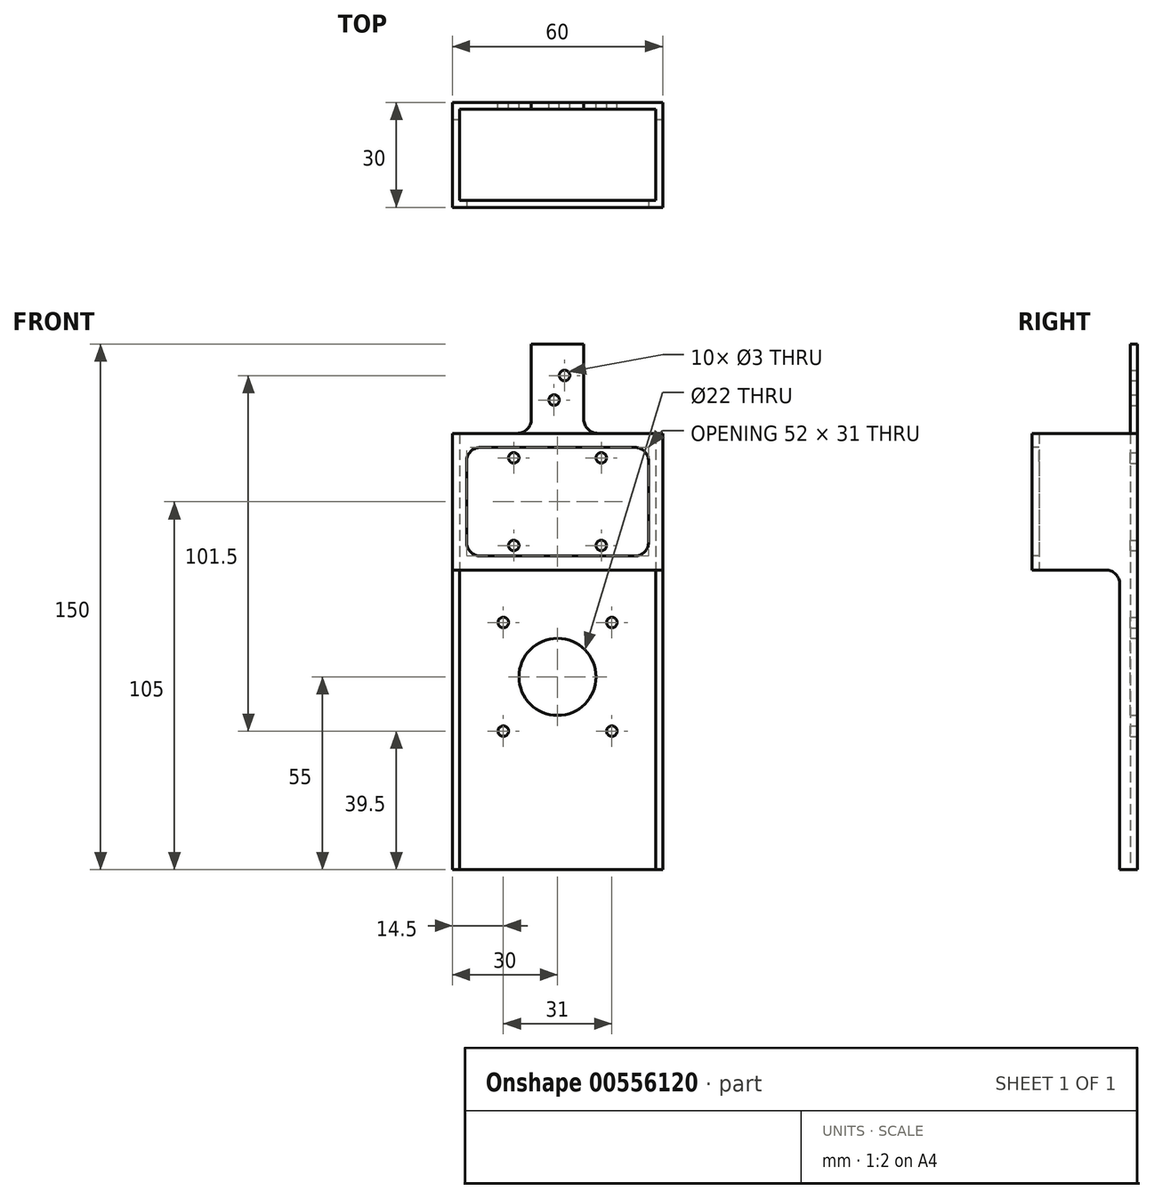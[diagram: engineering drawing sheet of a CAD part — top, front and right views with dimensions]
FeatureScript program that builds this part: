
annotation { "Feature Type Name" : "Feature", "Feature Type Description" : "" }
export const myFeature = defineFeature(function(context is Context, id is Id, definition is map)
    precondition{}
    {
        {
            var Q0;
            Q0=qCreatedBy(makeId("Top.planeOp"),FACE);
            var sketch = newSketch(context, id + "F0", { "sketchPlane" : qUnion([Q0])});
            skLineSegment(sketch, "E0.bottom", {"start": v(30, 15) * mm, "end": v(-30, 15) * mm});
            skLineSegment(sketch, "E0.top", {"start": v(30, -15) * mm, "end": v(-30, -15) * mm});
            skLineSegment(sketch, "E0.left", {"start": v(30, 15) * mm, "end": v(30, -15) * mm});
            skLineSegment(sketch, "E0.right", {"start": v(-30, 15) * mm, "end": v(-30, -15) * mm});
            skPoint(sketch, "E0.middle", {"position": v(0, 0) * mm});
            skSolve(sketch);
        }
        {
            var Q0;
            Q0 = qSketchRegion(id + "F0", true);
            extrude(context, id + "F1", {"entities" : qUnion([Q0]), "depth" : 150 * mm, "offsetDistance" : 25 * mm});
        }
        {
            var Q0;
            Q0=makeQuery(id+"F1.opExtrude","CAP_FACE",FACE,{"disambiguationData":[OSD([sQuery(id+"F0.wireOp",EDGE,"E0.bottom"),sQuery(id+"F0.wireOp",EDGE,"E0.top"),sQuery(id+"F0.wireOp",EDGE,"E0.left"),sQuery(id+"F0.wireOp",EDGE,"E0.right")])],"isStart":false});
            var Q1;
            Q1=makeQuery(id+"F1.opExtrude","CAP_FACE",FACE,{"disambiguationData":[OSD([sQuery(id+"F0.wireOp",EDGE,"E0.bottom"),sQuery(id+"F0.wireOp",EDGE,"E0.top"),sQuery(id+"F0.wireOp",EDGE,"E0.left"),sQuery(id+"F0.wireOp",EDGE,"E0.right")])],"isStart":true});
            shell(context, id + "F2", {"entities" : qUnion([Q0, Q1]), "thickness" : 2 * mm});
        }
        {
            var Q0;
            Q0=makeQuery(id+"F1.opExtrude","SWEPT_FACE",FACE,{"disambiguationData":[OSD([sQuery(id+"F0.wireOp",EDGE,"E0.bottom")])]});
            var sketch = newSketch(context, id + "F3", { "sketchPlane" : qUnion([Q0])});
            skLineSegment(sketch, "E1.bottom", {"start": v(12.5, 117.5) * mm, "end": v(-12.5, 117.5) * mm, "construction": true});
            skLineSegment(sketch, "E1.top", {"start": v(12.5, 92.5) * mm, "end": v(-12.5, 92.5) * mm, "construction": true});
            skLineSegment(sketch, "E1.left", {"start": v(12.5, 117.5) * mm, "end": v(12.5, 92.5) * mm, "construction": true});
            skLineSegment(sketch, "E1.right", {"start": v(-12.5, 117.5) * mm, "end": v(-12.5, 92.5) * mm, "construction": true});
            skPoint(sketch, "E1.middle", {"position": v(0, 105) * mm});
            skCircle(sketch, "E2", {"center": v(0, 55) * mm, "radius": 11 * mm});
            skLineSegment(sketch, "E3.bottom", {"start": v(15.5, 70.5) * mm, "end": v(-15.5, 70.5) * mm, "construction": true});
            skLineSegment(sketch, "E3.top", {"start": v(15.5, 39.5) * mm, "end": v(-15.5, 39.5) * mm, "construction": true});
            skLineSegment(sketch, "E3.left", {"start": v(15.5, 70.5) * mm, "end": v(15.5, 39.5) * mm, "construction": true});
            skLineSegment(sketch, "E3.right", {"start": v(-15.5, 70.5) * mm, "end": v(-15.5, 39.5) * mm, "construction": true});
            skLineSegment(sketch, "E4.top", {"start": v(-7.5, 125) * mm, "end": v(7.5, 125) * mm, "construction": true});
            skLineSegment(sketch, "E4.left", {"start": v(-7.5, 150) * mm, "end": v(-7.5, 125) * mm, "construction": true});
            skLineSegment(sketch, "E4.right", {"start": v(7.5, 150) * mm, "end": v(7.5, 125) * mm, "construction": true});
            skPoint(sketch, "E4.middle", {"position": v(0, 137.5) * mm});
            skLineSegment(sketch, "E5", {"start": v(1, 125) * mm, "end": v(1, 150) * mm, "construction": true});
            skLineSegment(sketch, "E6", {"start": v(-2, 125) * mm, "end": v(-2, 150) * mm, "construction": true});
            skPoint(sketch, "E7", {"position": v(-2, 141) * mm});
            skPoint(sketch, "E8", {"position": v(1, 134) * mm});
            skSolve(sketch);
        }
        {
            var Q0;
            Q0=sQuery(id+"F3.wireOp",VERTEX,"E1.right.start");
            var Q1;
            Q1=sQuery(id+"F3.wireOp",VERTEX,"E1.bottom.start");
            var Q2;
            Q2=sQuery(id+"F3.wireOp",VERTEX,"E1.right.end");
            var Q3;
            Q3=sQuery(id+"F3.wireOp",VERTEX,"E1.left.end");
            var Q4;
            Q4=makeQuery(id+"F1.opExtrude","SWEPT_BODY",BODY,{"disambiguationData":[OSD([sQuery(id+"F0.wireOp",EDGE,"E0.bottom"),sQuery(id+"F0.wireOp",EDGE,"E0.top"),sQuery(id+"F0.wireOp",EDGE,"E0.left"),sQuery(id+"F0.wireOp",EDGE,"E0.right")])]});
            hole(context, id + "F4", {"style" : HoleStyle.SIMPLE, "endStyle" : HoleEndStyle.THROUGH, "holeDiameter" : 3 * mm, "majorDiameter" : 5 * mm, "isTappedThrough" : true, "tappedDepth" : 12 * mm, "tapClearance" : 3, "startFromSketch" : true, "locations" : qUnion([Q0, Q1, Q2, Q3]), "scope" : qUnion([Q4])});
        }
        {
            var Q0;
            Q0=makeQuery(id+"F3.imprint","IMPRINT",FACE,{"disambiguationData":[TD([[makeQuery(id+"F3.imprint","IMPRINT",EDGE,{"derivedFrom":sQuery(id+"F3.wireOp",EDGE,"E2")}),1.0]])]});
            var Q1;
            Q1=makeQuery(id+"F2.opShell","OFFSET_FACE",FACE,{"disambiguationData":[OSD([sQuery(id+"F0.wireOp",EDGE,"E0.bottom")])]});
            extrude(context, id + "F5", {"entities" : qUnion([Q0]), "operationType" : NewBodyOperationType.REMOVE, "endBound" : BoundingType.THROUGH_ALL, "oppositeDirection" : true, "depth" : 25 * mm, "endBoundEntityFace" : qUnion([Q1]), "offsetDistance" : 25 * mm});
        }
        {
            var Q0;
            Q0=sQuery(id+"F3.wireOp",VERTEX,"E3.right.start");
            var Q1;
            Q1=sQuery(id+"F3.wireOp",VERTEX,"E3.left.start");
            var Q2;
            Q2=sQuery(id+"F3.wireOp",VERTEX,"E3.right.end");
            var Q3;
            Q3=sQuery(id+"F3.wireOp",VERTEX,"E3.left.end");
            var Q4;
            Q4=makeQuery(id+"F1.opExtrude","SWEPT_BODY",BODY,{"disambiguationData":[OSD([sQuery(id+"F0.wireOp",EDGE,"E0.bottom"),sQuery(id+"F0.wireOp",EDGE,"E0.top"),sQuery(id+"F0.wireOp",EDGE,"E0.left"),sQuery(id+"F0.wireOp",EDGE,"E0.right")])]});
            hole(context, id + "F6", {"style" : HoleStyle.SIMPLE, "endStyle" : HoleEndStyle.THROUGH, "holeDiameter" : 3 * mm, "majorDiameter" : 5 * mm, "isTappedThrough" : true, "tappedDepth" : 12 * mm, "tapClearance" : 3, "startFromSketch" : true, "locations" : qUnion([Q0, Q1, Q2, Q3]), "scope" : qUnion([Q4])});
        }
        {
            var Q0;
            Q0=sQuery(id+"F3.wireOp",VERTEX,"E7");
            var Q1;
            Q1=sQuery(id+"F3.wireOp",VERTEX,"E8");
            var Q2;
            Q2=makeQuery(id+"F1.opExtrude","SWEPT_BODY",BODY,{"disambiguationData":[OSD([sQuery(id+"F0.wireOp",EDGE,"E0.bottom"),sQuery(id+"F0.wireOp",EDGE,"E0.top"),sQuery(id+"F0.wireOp",EDGE,"E0.left"),sQuery(id+"F0.wireOp",EDGE,"E0.right")])]});
            hole(context, id + "F7", {"style" : HoleStyle.SIMPLE, "endStyle" : HoleEndStyle.THROUGH, "holeDiameter" : 3 * mm, "majorDiameter" : 5 * mm, "isTappedThrough" : true, "tappedDepth" : 12 * mm, "tapClearance" : 3, "startFromSketch" : true, "locations" : qUnion([Q0, Q1]), "scope" : qUnion([Q2])});
        }
        {
            var Q0;
            Q0=makeQuery(id+"F1.opExtrude","SWEPT_FACE",FACE,{"disambiguationData":[OSD([sQuery(id+"F0.wireOp",EDGE,"E0.top")])]});
            var sketch = newSketch(context, id + "F8", { "sketchPlane" : qUnion([Q0])});
            skLineSegment(sketch, "E9.bottom", {"start": v(26, 120.5) * mm, "end": v(-26, 120.5) * mm});
            skLineSegment(sketch, "E9.top", {"start": v(26, 89.5) * mm, "end": v(-26, 89.5) * mm});
            skLineSegment(sketch, "E9.left", {"start": v(26, 120.5) * mm, "end": v(26, 89.5) * mm});
            skLineSegment(sketch, "E9.right", {"start": v(-26, 120.5) * mm, "end": v(-26, 89.5) * mm});
            skPoint(sketch, "E9.middle", {"position": v(0, 105) * mm});
            skLineSegment(sketch, "E10", {"start": v(-30, 85.5) * mm, "end": v(30, 85.5) * mm});
            skLineSegment(sketch, "E11", {"start": v(-30, 124.5) * mm, "end": v(30, 124.5) * mm});
            skLineSegment(sketch, "E12", {"start": v(-7.5, 124.5) * mm, "end": v(-7.5, 150) * mm});
            skLineSegment(sketch, "E13", {"start": v(7.5, 124.5) * mm, "end": v(7.5, 150) * mm});
            skSolve(sketch);
        }
        {
            var Q0;
            Q0=makeQuery(id+"F8.imprint","IMPRINT",FACE,{"disambiguationData":[TD([[makeQuery(id+"F8.imprint","IMPRINT",EDGE,{"derivedFrom":sQuery(id+"F8.wireOp",EDGE,"E9.bottom")}),1.0]])]});
            var Q1;
            {var subQ5=sQuery(id+"F8.wireOp",EDGE,"E10");Q1=makeQuery(id+"F8.imprint","IMPRINT",FACE,{"disambiguationData":[TD([[makeQuery(id+"F8.imprint","IMPRINT",EDGE,{"derivedFrom":subQ5}),-1.0]])]});}
            var Q2;
            {var subQ3=sQuery(id+"F8.wireOp",EDGE,"E12");Q2=makeQuery(id+"F8.imprint","IMPRINT",FACE,{"disambiguationData":[TD([[makeQuery(id+"F8.imprint","IMPRINT",EDGE,{"derivedFrom":subQ3}),-1.0]])]});}
            var Q3;
            {var subQ4=sQuery(id+"F8.wireOp",EDGE,"E13");Q3=makeQuery(id+"F8.imprint","IMPRINT",FACE,{"disambiguationData":[TD([[makeQuery(id+"F8.imprint","IMPRINT",EDGE,{"derivedFrom":subQ4}),-1.0]])]});}
            var Q4;
            {var subQ4=sQuery(id+"F8.wireOp",EDGE,"E12");Q4=makeQuery(id+"F8.imprint","IMPRINT",FACE,{"disambiguationData":[TD([[makeQuery(id+"F8.imprint","IMPRINT",EDGE,{"derivedFrom":subQ4}),1.0]])]});}
            extrude(context, id + "F9", {"entities" : qUnion([Q0, Q1, Q2, Q3, Q4]), "operationType" : NewBodyOperationType.REMOVE, "oppositeDirection" : true, "depth" : 25 * mm, "offsetDistance" : 25 * mm});
        }
        {
            var Q0;
            {var subQ4=sQuery(id+"F8.wireOp",EDGE,"E12");Q0=makeQuery(id+"F8.imprint","IMPRINT",FACE,{"disambiguationData":[TD([[makeQuery(id+"F8.imprint","IMPRINT",EDGE,{"derivedFrom":subQ4}),1.0]])]});}
            var Q1;
            {var subQ4=sQuery(id+"F8.wireOp",EDGE,"E13");Q1=makeQuery(id+"F8.imprint","IMPRINT",FACE,{"disambiguationData":[TD([[makeQuery(id+"F8.imprint","IMPRINT",EDGE,{"derivedFrom":subQ4}),-1.0]])]});}
            extrude(context, id + "F10", {"entities" : qUnion([Q0, Q1]), "operationType" : NewBodyOperationType.REMOVE, "endBound" : BoundingType.THROUGH_ALL, "oppositeDirection" : true, "depth" : 25 * mm, "offsetDistance" : 25 * mm});
        }
        {
            var Q0;
            {var subQ0=sQuery(id+"F0.wireOp",EDGE,"E0.right");var subQ1=sQuery(id+"F8.wireOp",EDGE,"E10");Q0=makeQuery(id+"F9.boolean.opBoolean","COPY",EDGE,{"disambiguationData":[TD([makeQuery(id+"F1.opExtrude","SWEPT_FACE",FACE,{"disambiguationData":[OSD([subQ0])]})])],"derivedFrom":makeQuery(id+"F9.opExtrude","CAP_EDGE",EDGE,{"disambiguationData":[OSD([subQ1])],"isStart":false})});}
            var Q1;
            {var subQ0=sQuery(id+"F0.wireOp",EDGE,"E0.left");var subQ1=sQuery(id+"F8.wireOp",EDGE,"E10");Q1=makeQuery(id+"F9.boolean.opBoolean","COPY",EDGE,{"disambiguationData":[TD([makeQuery(id+"F1.opExtrude","SWEPT_FACE",FACE,{"disambiguationData":[OSD([subQ0])]})])],"derivedFrom":makeQuery(id+"F9.opExtrude","CAP_EDGE",EDGE,{"disambiguationData":[OSD([subQ1])],"isStart":false})});}
            var Q2;
            Q2=makeQuery(id+"F9.boolean.opBoolean","COPY",EDGE,{"derivedFrom":makeQuery(id+"F9.opExtrude","SWEPT_EDGE",EDGE,{"disambiguationData":[OSD([sQuery(id+"F8.wireOp",EDGE,"E9.bottom"),sQuery(id+"F8.wireOp",EDGE,"E9.right")])]})});
            var Q3;
            Q3=makeQuery(id+"F9.boolean.opBoolean","COPY",EDGE,{"derivedFrom":makeQuery(id+"F9.opExtrude","SWEPT_EDGE",EDGE,{"disambiguationData":[OSD([sQuery(id+"F8.wireOp",EDGE,"E9.bottom"),sQuery(id+"F8.wireOp",EDGE,"E9.left")])]})});
            var Q4;
            Q4=makeQuery(id+"F9.boolean.opBoolean","COPY",EDGE,{"derivedFrom":makeQuery(id+"F9.opExtrude","SWEPT_EDGE",EDGE,{"disambiguationData":[OSD([sQuery(id+"F8.wireOp",EDGE,"E9.top"),sQuery(id+"F8.wireOp",EDGE,"E9.left")])]})});
            var Q5;
            Q5=makeQuery(id+"F9.boolean.opBoolean","COPY",EDGE,{"derivedFrom":makeQuery(id+"F9.opExtrude","SWEPT_EDGE",EDGE,{"disambiguationData":[OSD([sQuery(id+"F8.wireOp",EDGE,"E9.top"),sQuery(id+"F8.wireOp",EDGE,"E9.right")])]})});
            var Q6;
            {var subQ0=sQuery(id+"F0.wireOp",EDGE,"E0.bottom");var subQ1=sQuery(id+"F8.wireOp",EDGE,"E11");var subQ2=sQuery(id+"F8.wireOp",EDGE,"E12");Q6=makeQuery(id+"F10.boolean.opBoolean","COPY",EDGE,{"disambiguationData":[TD([makeQuery(id+"F1.opExtrude","SWEPT_FACE",FACE,{"disambiguationData":[OSD([subQ0])]})])],"derivedFrom":makeQuery(id+"F10.opExtrude","SWEPT_EDGE",EDGE,{"disambiguationData":[OSD([subQ1,subQ2])]})});}
            var Q7;
            {var subQ0=sQuery(id+"F0.wireOp",EDGE,"E0.top");var subQ1=sQuery(id+"F8.wireOp",EDGE,"E11");var subQ2=sQuery(id+"F8.wireOp",EDGE,"E12");Q7=makeQuery(id+"F10.boolean.opBoolean","COPY",EDGE,{"disambiguationData":[TD([makeQuery(id+"F1.opExtrude","SWEPT_FACE",FACE,{"disambiguationData":[OSD([subQ0])]})])],"derivedFrom":makeQuery(id+"F10.opExtrude","SWEPT_EDGE",EDGE,{"disambiguationData":[OSD([subQ1,subQ2])]})});}
            var Q8;
            {var subQ0=sQuery(id+"F0.wireOp",EDGE,"E0.top");var subQ1=sQuery(id+"F8.wireOp",EDGE,"E12");Q8=makeQuery(id+"F10.boolean.opBoolean","COPY",EDGE,{"disambiguationData":[TD([makeQuery(id+"F1.opExtrude","SWEPT_FACE",FACE,{"disambiguationData":[OSD([subQ0])]})])],"derivedFrom":makeQuery(id+"F10.opExtrude","SWEPT_EDGE",EDGE,{"disambiguationData":[OSD([subQ0,subQ1])]})});}
            var Q9;
            {var subQ0=sQuery(id+"F0.wireOp",EDGE,"E0.bottom");var subQ1=sQuery(id+"F0.wireOp",EDGE,"E0.top");var subQ2=sQuery(id+"F8.wireOp",EDGE,"E12");Q9=makeQuery(id+"F10.boolean.opBoolean","COPY",EDGE,{"disambiguationData":[TD([makeQuery(id+"F1.opExtrude","SWEPT_FACE",FACE,{"disambiguationData":[OSD([subQ0])]})])],"derivedFrom":makeQuery(id+"F10.opExtrude","SWEPT_EDGE",EDGE,{"disambiguationData":[OSD([subQ1,subQ2])]})});}
            var Q10;
            {var subQ0=sQuery(id+"F0.wireOp",EDGE,"E0.bottom");var subQ1=sQuery(id+"F0.wireOp",EDGE,"E0.top");var subQ2=sQuery(id+"F8.wireOp",EDGE,"E13");Q10=makeQuery(id+"F10.boolean.opBoolean","COPY",EDGE,{"disambiguationData":[TD([makeQuery(id+"F1.opExtrude","SWEPT_FACE",FACE,{"disambiguationData":[OSD([subQ0])]})])],"derivedFrom":makeQuery(id+"F10.opExtrude","SWEPT_EDGE",EDGE,{"disambiguationData":[OSD([subQ1,subQ2])]})});}
            var Q11;
            {var subQ0=sQuery(id+"F0.wireOp",EDGE,"E0.top");var subQ1=sQuery(id+"F8.wireOp",EDGE,"E13");Q11=makeQuery(id+"F10.boolean.opBoolean","COPY",EDGE,{"disambiguationData":[TD([makeQuery(id+"F1.opExtrude","SWEPT_FACE",FACE,{"disambiguationData":[OSD([subQ0])]})])],"derivedFrom":makeQuery(id+"F10.opExtrude","SWEPT_EDGE",EDGE,{"disambiguationData":[OSD([subQ0,subQ1])]})});}
            var Q12;
            {var subQ0=sQuery(id+"F0.wireOp",EDGE,"E0.bottom");var subQ1=sQuery(id+"F8.wireOp",EDGE,"E11");var subQ2=sQuery(id+"F8.wireOp",EDGE,"E13");Q12=makeQuery(id+"F10.boolean.opBoolean","COPY",EDGE,{"disambiguationData":[TD([makeQuery(id+"F1.opExtrude","SWEPT_FACE",FACE,{"disambiguationData":[OSD([subQ0])]})])],"derivedFrom":makeQuery(id+"F10.opExtrude","SWEPT_EDGE",EDGE,{"disambiguationData":[OSD([subQ1,subQ2])]})});}
            var Q13;
            {var subQ0=sQuery(id+"F0.wireOp",EDGE,"E0.top");var subQ1=sQuery(id+"F8.wireOp",EDGE,"E11");var subQ2=sQuery(id+"F8.wireOp",EDGE,"E13");Q13=makeQuery(id+"F10.boolean.opBoolean","COPY",EDGE,{"disambiguationData":[TD([makeQuery(id+"F1.opExtrude","SWEPT_FACE",FACE,{"disambiguationData":[OSD([subQ0])]})])],"derivedFrom":makeQuery(id+"F10.opExtrude","SWEPT_EDGE",EDGE,{"disambiguationData":[OSD([subQ1,subQ2])]})});}
            var Q14;
            {var subQ1=sQuery(id+"F0.wireOp",EDGE,"E0.left");var subQ2=sQuery(id+"F0.wireOp",EDGE,"E0.top");Q14=makeQuery(id+"F9.boolean.opBoolean","COPY",EDGE,{"disambiguationData":[TD([makeQuery(id+"F1.opExtrude","SWEPT_FACE",FACE,{"disambiguationData":[OSD([subQ1])]})])],"derivedFrom":makeQuery(id+"F9.opExtrude","CAP_EDGE",EDGE,{"disambiguationData":[OSD([subQ2])],"isStart":false})});}
            fillet(context, id + "F11", {"entities" : qUnion([Q0, Q1, Q2, Q3, Q4, Q5, Q6, Q7, Q8, Q9, Q10, Q11, Q12, Q13, Q14]), "radius" : 4 * mm, "tangentPropagation" : true, "allowEdgeOverflow" : false});
        }
    });
